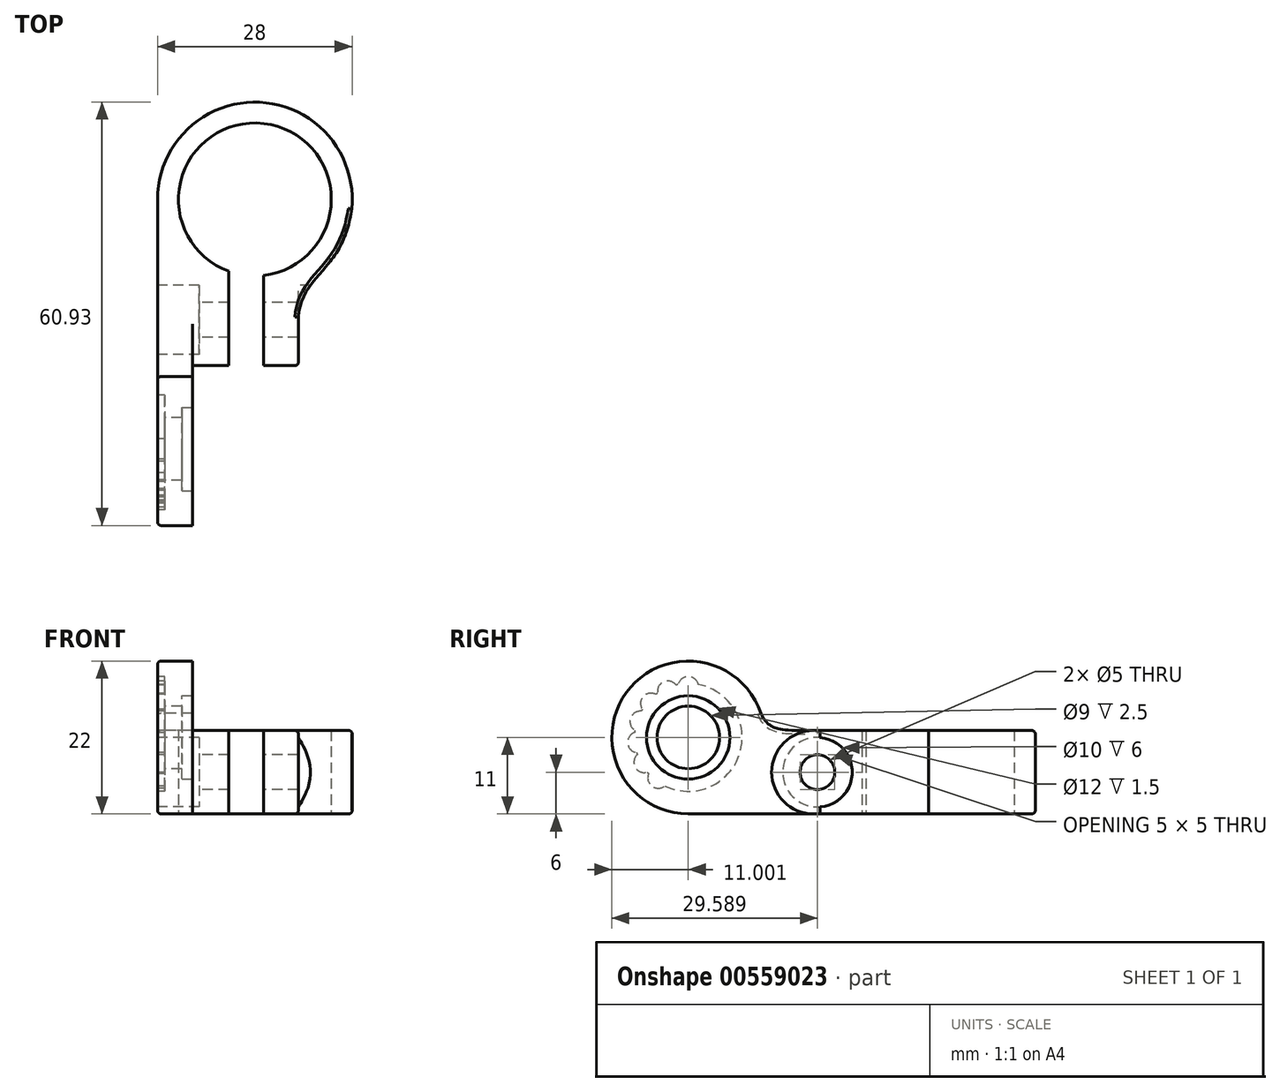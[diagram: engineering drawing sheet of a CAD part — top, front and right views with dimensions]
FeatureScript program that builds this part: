
annotation { "Feature Type Name" : "Feature", "Feature Type Description" : "" }
export const myFeature = defineFeature(function(context is Context, id is Id, definition is map)
    precondition{}
    {
        {
            var Q0;
            Q0=qCreatedBy(makeId("Top.planeOp"),FACE);
            var sketch = newSketch(context, id + "F0", { "sketchPlane" : qUnion([Q0])});
            skArc(sketch, "E0", {"start": v(1.25, -10.93) * mm, "mid": v(1.28, 10.92) * mm, "end": v(-3.75, -10.34) * mm});
            skArc(sketch, "E1", {"start": v(13.93, -1.37) * mm, "mid": v(0.69, 13.98) * mm, "end": v(-14, 0) * mm});
            skLineSegment(sketch, "E2", {"start": v(-14, 0) * mm, "end": v(-14, -23.93) * mm});
            skFitSpline(sketch, "E3", {"points": [v(13.93, -1.37) * mm, v(6.25, -16.94) * mm], "startDerivative": vector(-3.88, -27.33) * mm, "endDerivative": vector(-1.43, -19.02) * mm});
            skLineSegment(sketch, "E4", {"start": v(6.25, -16.94) * mm, "end": v(6.25, -23.93) * mm});
            skLineSegment(sketch, "E5", {"start": v(6.25, -23.93) * mm, "end": v(1.25, -23.93) * mm});
            skLineSegment(sketch, "E6", {"start": v(1.25, -23.93) * mm, "end": v(1.25, -10.93) * mm});
            skLineSegment(sketch, "E7", {"start": v(-3.75, -10.34) * mm, "end": v(-3.75, -23.93) * mm});
            skLineSegment(sketch, "E8", {"start": v(-3.75, -23.93) * mm, "end": v(-14, -23.93) * mm});
            skSolve(sketch);
        }
        {
            var Q0;
            Q0=makeQuery(id+"F0.imprint","IMPRINT",FACE,{"disambiguationData":[TD([[makeQuery(id+"F0.imprint","IMPRINT",EDGE,{"derivedFrom":sQuery(id+"F0.wireOp",EDGE,"E0")}),-1.0]])]});
            extrude(context, id + "F1", {"entities" : qUnion([Q0]), "endBound" : BoundingType.SYMMETRIC, "depth" : 12 * mm, "offsetDistance" : 25 * mm});
        }
        {
            var Q0;
            Q0=makeQuery(id+"F1.opExtrude","SWEPT_FACE",FACE,{"disambiguationData":[OSD([sQuery(id+"F0.wireOp",EDGE,"E2")])]});
            var sketch = newSketch(context, id + "F2", { "sketchPlane" : qUnion([Q0])});
            skLineSegment(sketch, "E9", {"start": v(23.93, -6) * mm, "end": v(35.93, -6) * mm});
            skCircle(sketch, "E10", {"center": v(35.93, 5) * mm, "radius": 11 * mm});
            skFitSpline(sketch, "E11", {"points": [v(19.13, 6) * mm, v(24.07, 6.72) * mm, v(26.04, 9.82) * mm], "startDerivative": vector(19.83, 0) * mm, "endDerivative": vector(5.27, 14.74) * mm});
            skSolve(sketch);
        }
        {
            var Q0;
            Q0 = qSketchRegion(id + "F2", true);
            var Q1;
            {var subQ7=sQuery(id+"F2.wireOp",EDGE,"E9");Q1=makeQuery(id+"F2.imprint","IMPRINT",FACE,{"disambiguationData":[TD([[makeQuery(id+"F2.imprint","IMPRINT",EDGE,{"derivedFrom":subQ7}),1.0]])]});}
            extrude(context, id + "F3", {"entities" : qUnion([Q0, Q1]), "operationType" : NewBodyOperationType.ADD, "oppositeDirection" : true, "depth" : 5 * mm, "offsetDistance" : 25 * mm});
        }
        {
            var Q0;
            {var subQ0=sQuery(id+"F0.wireOp",EDGE,"E2");Q0=makeQuery(id+"F3.boolean.opBoolean","MERGE",FACE,{"derivedFrom":[makeQuery(id+"F1.opExtrude","SWEPT_FACE",FACE,{"disambiguationData":[OSD([subQ0])]}),makeQuery(id+"F3.opExtrude","CAP_FACE",FACE,{"disambiguationData":[OSD([subQ0,sQuery(id+"F0.wireOp",EDGE,"E8"),sQuery(id+"F2.wireOp",EDGE,"E9"),sQuery(id+"F2.wireOp",EDGE,"E10"),sQuery(id+"F2.wireOp",EDGE,"E11")])],"isStart":true})]});}
            var sketch = newSketch(context, id + "F4", { "sketchPlane" : qUnion([Q0])});
            skCircle(sketch, "E12", {"center": v(17.34, 0) * mm, "radius": 2.5 * mm});
            skCircle(sketch, "E13", {"center": v(17.34, 0) * mm, "radius": 5 * mm});
            skSolve(sketch);
        }
        {
            var Q0;
            Q0=makeQuery(id+"F4.imprint","IMPRINT",FACE,{"disambiguationData":[TD([[makeQuery(id+"F4.imprint","IMPRINT",EDGE,{"derivedFrom":sQuery(id+"F4.wireOp",EDGE,"E12")}),1.0]])]});
            extrude(context, id + "F5", {"entities" : qUnion([Q0]), "operationType" : NewBodyOperationType.REMOVE, "endBound" : BoundingType.THROUGH_ALL, "oppositeDirection" : true, "depth" : 25 * mm, "offsetDistance" : 25 * mm});
        }
        {
            var Q0;
            Q0 = qSketchRegion(id + "F4", true);
            extrude(context, id + "F6", {"entities" : qUnion([Q0]), "operationType" : NewBodyOperationType.REMOVE, "oppositeDirection" : true, "depth" : 6 * mm, "offsetDistance" : 25 * mm});
        }
        {
            var Q0;
            Q0=makeQuery(id+"F1.opExtrude","SWEPT_FACE",FACE,{"disambiguationData":[OSD([sQuery(id+"F0.wireOp",EDGE,"E4")])]});
            var sketch = newSketch(context, id + "F7", { "sketchPlane" : qUnion([Q0])});
            skCircle(sketch, "E14", {"center": v(-17.34, 0) * mm, "radius": 5 * mm});
            skSolve(sketch);
        }
        {
            var Q0;
            Q0 = qSketchRegion(id + "F7", true);
            extrude(context, id + "F8", {"entities" : qUnion([Q0]), "operationType" : NewBodyOperationType.REMOVE, "endBound" : BoundingType.THROUGH_ALL, "depth" : 25 * mm, "offsetDistance" : 25 * mm});
        }
        {
            var Q0;
            {var subQ0=sQuery(id+"F0.wireOp",EDGE,"E2");Q0=makeQuery(id+"F3.boolean.opBoolean","MERGE",FACE,{"derivedFrom":[makeQuery(id+"F1.opExtrude","SWEPT_FACE",FACE,{"disambiguationData":[OSD([subQ0])]}),makeQuery(id+"F3.opExtrude","CAP_FACE",FACE,{"disambiguationData":[OSD([subQ0,sQuery(id+"F0.wireOp",EDGE,"E8"),sQuery(id+"F2.wireOp",EDGE,"E9"),sQuery(id+"F2.wireOp",EDGE,"E10"),sQuery(id+"F2.wireOp",EDGE,"E11")])],"isStart":true})]});}
            var sketch = newSketch(context, id + "F9", { "sketchPlane" : qUnion([Q0])});
            skCircle(sketch, "E15", {"center": v(35.93, 5) * mm, "radius": 4.5 * mm});
            skArc(sketch, "E16", {"start": v(39.31, -1.97) * mm, "mid": v(41.16, -2.01) * mm, "end": v(41.65, -0.23) * mm});
            skArc(sketch, "E17", {"start": v(34.47, 12.61) * mm, "mid": v(28.57, 2.56) * mm, "end": v(39.31, -1.97) * mm});
            skArc(sketch, "E18.trimOffspring", {"start": v(37.38, 12.61) * mm, "mid": v(35.93, 13.75) * mm, "end": v(34.47, 12.61) * mm});
            skArc(sketch, "E19.trimOffspring", {"start": v(37.68, 12.55) * mm, "mid": v(37.53, 12.58) * mm, "end": v(37.38, 12.61) * mm});
            skArc(sketch, "E20.trimOffspring", {"start": v(40.34, 11.37) * mm, "mid": v(39.47, 13) * mm, "end": v(37.68, 12.55) * mm});
            skArc(sketch, "E21.trimOffspring", {"start": v(40.59, 11.2) * mm, "mid": v(40.46, 11.28) * mm, "end": v(40.34, 11.37) * mm});
            skArc(sketch, "E22.trimOffspring", {"start": v(42.54, 9.04) * mm, "mid": v(42.4, 10.88) * mm, "end": v(40.59, 11.2) * mm});
            skArc(sketch, "E23.trimOffspring", {"start": v(42.7, 8.78) * mm, "mid": v(42.62, 8.9) * mm, "end": v(42.54, 9.04) * mm});
            skArc(sketch, "E24.trimOffspring", {"start": v(43.61, 6.02) * mm, "mid": v(44.23, 7.76) * mm, "end": v(42.7, 8.78) * mm});
            skArc(sketch, "E25.trimOffspring", {"start": v(43.65, 5.72) * mm, "mid": v(43.63, 5.87) * mm, "end": v(43.61, 6.02) * mm});
            skArc(sketch, "E26.trimOffspring", {"start": v(43.37, 2.82) * mm, "mid": v(44.64, 4.16) * mm, "end": v(43.65, 5.72) * mm});
            skArc(sketch, "E27.trimOffspring", {"start": v(43.27, 2.53) * mm, "mid": v(43.32, 2.67) * mm, "end": v(43.37, 2.82) * mm});
            skArc(sketch, "E28.trimOffspring", {"start": v(41.65, -0.23) * mm, "mid": v(41.75, -0.12) * mm, "end": v(41.85, 0) * mm});
            skArc(sketch, "E29.trimOffspring", {"start": v(41.85, 0) * mm, "mid": v(43.55, 0.7) * mm, "end": v(43.27, 2.53) * mm});
            skSolve(sketch);
        }
        {
            var Q0;
            Q0 = qSketchRegion(id + "F9", true);
            var Q1;
            Q1=makeQuery(id+"F9.imprint","IMPRINT",FACE,{"disambiguationData":[TD([[makeQuery(id+"F9.imprint","IMPRINT",EDGE,{"derivedFrom":sQuery(id+"F9.wireOp",EDGE,"E15")}),-1.0]])]});
            var Q2;
            {var subQ0=sQuery(id+"F9.wireOp",EDGE,"fbPnNNW9-PMxX-t2PX-k55c-5nS3xq7yzQ3p");var subQ1=sQuery(id+"F9.wireOp",EDGE,"QZW2g8Qc-ykgd-0s4w-dwwp-Ej2pU9XGU9IL");var subQ2=makeQuery(id+"F9.imprint","INTERSECT",VERTEX,{"disambiguationData":[OD(0.0)],"derivedFrom":[subQ1,subQ0]});Q2=makeQuery(id+"F9.imprint","IMPRINT",FACE,{"disambiguationData":[TD([[makeQuery(id+"F9.imprint","IMPRINT",EDGE,{"disambiguationData":[TD([[subQ2,1.0]])],"derivedFrom":subQ1}),1.0]])]});}
            var Q3;
            {var subQ0=sQuery(id+"F9.wireOp",EDGE,"yLPPB9Eb-vPD5-GLMI-5RPp-IEYl9C8609n6");var subQ1=sQuery(id+"F9.wireOp",EDGE,"QZW2g8Qc-ykgd-0s4w-dwwp-Ej2pU9XGU9IL");var subQ2=makeQuery(id+"F9.imprint","INTERSECT",VERTEX,{"disambiguationData":[OD(0.0)],"derivedFrom":[subQ1,subQ0]});Q3=makeQuery(id+"F9.imprint","IMPRINT",FACE,{"disambiguationData":[TD([[makeQuery(id+"F9.imprint","IMPRINT",EDGE,{"disambiguationData":[TD([[subQ2,-1.0]])],"derivedFrom":subQ1}),1.0]])]});}
            var Q4;
            {var subQ0=sQuery(id+"F9.wireOp",EDGE,"E16");var subQ1=sQuery(id+"F9.wireOp",EDGE,"QZW2g8Qc-ykgd-0s4w-dwwp-Ej2pU9XGU9IL");var subQ2=makeQuery(id+"F9.imprint","INTERSECT",VERTEX,{"disambiguationData":[OD(0.0)],"derivedFrom":[subQ1,subQ0]});Q4=makeQuery(id+"F9.imprint","IMPRINT",FACE,{"disambiguationData":[TD([[makeQuery(id+"F9.imprint","IMPRINT",EDGE,{"disambiguationData":[TD([[subQ2,-1.0]])],"derivedFrom":subQ1}),1.0]])]});}
            var Q5;
            {var subQ0=sQuery(id+"F9.wireOp",EDGE,"8HanLNPq-ip7b-hnWU-B5sB-qfkkRq3HLb1e");var subQ1=sQuery(id+"F9.wireOp",EDGE,"QZW2g8Qc-ykgd-0s4w-dwwp-Ej2pU9XGU9IL");var subQ2=makeQuery(id+"F9.imprint","INTERSECT",VERTEX,{"disambiguationData":[OD(0.0)],"derivedFrom":[subQ1,subQ0]});Q5=makeQuery(id+"F9.imprint","IMPRINT",FACE,{"disambiguationData":[TD([[makeQuery(id+"F9.imprint","IMPRINT",EDGE,{"disambiguationData":[TD([[subQ2,-1.0]])],"derivedFrom":subQ1}),1.0]])]});}
            var Q6;
            {var subQ0=sQuery(id+"F9.wireOp",EDGE,"G71yeFtQ-zlGd-nF3p-KKE1-QoE51yrrW6Fs");var subQ1=sQuery(id+"F9.wireOp",EDGE,"QZW2g8Qc-ykgd-0s4w-dwwp-Ej2pU9XGU9IL");var subQ2=makeQuery(id+"F9.imprint","INTERSECT",VERTEX,{"disambiguationData":[OD(0.0)],"derivedFrom":[subQ1,subQ0]});Q6=makeQuery(id+"F9.imprint","IMPRINT",FACE,{"disambiguationData":[TD([[makeQuery(id+"F9.imprint","IMPRINT",EDGE,{"disambiguationData":[TD([[subQ2,-1.0]])],"derivedFrom":subQ1}),1.0]])]});}
            var Q7;
            {var subQ0=sQuery(id+"F9.wireOp",EDGE,"8UitzcVi-eXTD-MqgP-6Jej-oq9UdkX41hCN");var subQ1=sQuery(id+"F9.wireOp",EDGE,"QZW2g8Qc-ykgd-0s4w-dwwp-Ej2pU9XGU9IL");var subQ2=makeQuery(id+"F9.imprint","INTERSECT",VERTEX,{"disambiguationData":[OD(0.0)],"derivedFrom":[subQ1,subQ0]});Q7=makeQuery(id+"F9.imprint","IMPRINT",FACE,{"disambiguationData":[TD([[makeQuery(id+"F9.imprint","IMPRINT",EDGE,{"disambiguationData":[TD([[subQ2,-1.0]])],"derivedFrom":subQ1}),1.0]])]});}
            var Q8;
            {var subQ0=sQuery(id+"F9.wireOp",EDGE,"bhop12Ne-FdNS-1RI7-3D0L-sXM0d9xyUDR8");var subQ1=sQuery(id+"F9.wireOp",EDGE,"QZW2g8Qc-ykgd-0s4w-dwwp-Ej2pU9XGU9IL");var subQ2=makeQuery(id+"F9.imprint","INTERSECT",VERTEX,{"disambiguationData":[OD(0.0)],"derivedFrom":[subQ1,subQ0]});Q8=makeQuery(id+"F9.imprint","IMPRINT",FACE,{"disambiguationData":[TD([[makeQuery(id+"F9.imprint","IMPRINT",EDGE,{"disambiguationData":[TD([[subQ2,-1.0]])],"derivedFrom":subQ1}),1.0]])]});}
            extrude(context, id + "F10", {"entities" : qUnion([Q0, Q1, Q2, Q3, Q4, Q5, Q6, Q7, Q8]), "operationType" : NewBodyOperationType.REMOVE, "oppositeDirection" : true, "depth" : 1 * mm, "offsetDistance" : 25 * mm});
        }
        {
            var Q0;
            {var subQ0=sQuery(id+"F0.wireOp",EDGE,"E2");Q0=makeQuery(id+"F10.boolean.opBoolean","SPLIT",FACE,{"disambiguationData":[TD([makeQuery(id+"F10.opExtrude","SWEPT_FACE",FACE,{"disambiguationData":[OSD([sQuery(id+"F9.wireOp",EDGE,"E15")])]})])],"derivedFrom":makeQuery(id+"F3.boolean.opBoolean","MERGE",FACE,{"derivedFrom":[makeQuery(id+"F1.opExtrude","SWEPT_FACE",FACE,{"disambiguationData":[OSD([subQ0])]}),makeQuery(id+"F3.opExtrude","CAP_FACE",FACE,{"disambiguationData":[OSD([subQ0,sQuery(id+"F0.wireOp",EDGE,"E8"),sQuery(id+"F2.wireOp",EDGE,"E9"),sQuery(id+"F2.wireOp",EDGE,"E10"),sQuery(id+"F2.wireOp",EDGE,"E11")])],"isStart":true})]})});}
            extrude(context, id + "F11", {"entities" : qUnion([Q0]), "operationType" : NewBodyOperationType.REMOVE, "endBound" : BoundingType.THROUGH_ALL, "oppositeDirection" : true, "depth" : 25 * mm, "offsetDistance" : 25 * mm});
        }
        {
            var Q0;
            Q0=makeQuery(id+"F1.opExtrude","CAP_EDGE",EDGE,{"disambiguationData":[OSD([sQuery(id+"F0.wireOp",EDGE,"E5")])],"isStart":true});
            var Q1;
            Q1=makeQuery(id+"F1.opExtrude","CAP_EDGE",EDGE,{"disambiguationData":[OSD([sQuery(id+"F0.wireOp",EDGE,"E8")])],"isStart":true});
            var Q2;
            Q2=makeQuery(id+"F1.opExtrude","CAP_EDGE",EDGE,{"disambiguationData":[OSD([sQuery(id+"F0.wireOp",EDGE,"E8")])],"isStart":false});
            var Q3;
            Q3=makeQuery(id+"F1.opExtrude","CAP_EDGE",EDGE,{"disambiguationData":[OSD([sQuery(id+"F0.wireOp",EDGE,"E5")])],"isStart":false});
            fillet(context, id + "F12", {"entities" : qUnion([Q0, Q1, Q2, Q3]), "radius" : 6 * mm, "tangentPropagation" : true, "allowEdgeOverflow" : false});
        }
        {
            var Q0;
            Q0=makeQuery(id+"F12.opFillet","BLEND_EDGE",EDGE,{"blendedFrom":[makeQuery(id+"F1.opExtrude","CAP_EDGE",EDGE,{"disambiguationData":[OSD([sQuery(id+"F0.wireOp",EDGE,"E5")])],"isStart":false}),makeQuery(id+"F8.boolean.opBoolean","MERGE",FACE,{"derivedFrom":[makeQuery(id+"F1.opExtrude","SWEPT_FACE",FACE,{"disambiguationData":[OSD([sQuery(id+"F0.wireOp",EDGE,"E4")])]}),makeQuery(id+"F8.opExtrude","CAP_FACE",FACE,{"disambiguationData":[OSD([sQuery(id+"F7.wireOp",EDGE,"E14")])],"isStart":true})]})],"blendedInto":[makeQuery(id+"F8.boolean.opBoolean","MERGE",FACE,{"derivedFrom":[makeQuery(id+"F1.opExtrude","SWEPT_FACE",FACE,{"disambiguationData":[OSD([sQuery(id+"F0.wireOp",EDGE,"E4")])]}),makeQuery(id+"F8.opExtrude","CAP_FACE",FACE,{"disambiguationData":[OSD([sQuery(id+"F7.wireOp",EDGE,"E14")])],"isStart":true})]})]});
            var Q1;
            Q1=makeQuery(id+"F1.opExtrude","CAP_EDGE",EDGE,{"disambiguationData":[OSD([sQuery(id+"F0.wireOp",EDGE,"E4")])],"isStart":true});
            var Q2;
            Q2=makeQuery(id+"F1.opExtrude","CAP_EDGE",EDGE,{"disambiguationData":[OSD([sQuery(id+"F0.wireOp",EDGE,"E3")])],"isStart":true});
            var Q3;
            Q3=makeQuery(id+"F1.opExtrude","CAP_EDGE",EDGE,{"disambiguationData":[OSD([sQuery(id+"F0.wireOp",EDGE,"E4")])],"isStart":false});
            var Q4;
            Q4=makeQuery(id+"F1.opExtrude","CAP_EDGE",EDGE,{"disambiguationData":[OSD([sQuery(id+"F0.wireOp",EDGE,"E3")])],"isStart":false});
            var Q5;
            Q5=makeQuery(id+"F1.opExtrude","CAP_EDGE",EDGE,{"disambiguationData":[OSD([sQuery(id+"F0.wireOp",EDGE,"E1")])],"isStart":true});
            var Q6;
            Q6=makeQuery(id+"F1.opExtrude","CAP_EDGE",EDGE,{"disambiguationData":[OSD([sQuery(id+"F0.wireOp",EDGE,"E1")])],"isStart":false});
            var Q7;
            Q7=makeQuery(id+"F3.boolean.opBoolean","MERGE",EDGE,{"derivedFrom":[makeQuery(id+"F1.opExtrude","CAP_EDGE",EDGE,{"disambiguationData":[OSD([sQuery(id+"F0.wireOp",EDGE,"E2")])],"isStart":true}),makeQuery(id+"F3.opExtrude","CAP_EDGE",EDGE,{"disambiguationData":[OSD([sQuery(id+"F2.wireOp",EDGE,"E9")])],"isStart":true})]});
            var Q8;
            Q8=makeQuery(id+"F3.opExtrude","CAP_EDGE",EDGE,{"disambiguationData":[OSD([sQuery(id+"F2.wireOp",EDGE,"E10")])],"isStart":true});
            var Q9;
            Q9=makeQuery(id+"F3.opExtrude","CAP_EDGE",EDGE,{"disambiguationData":[OSD([sQuery(id+"F2.wireOp",EDGE,"E11")])],"isStart":true});
            var Q10;
            Q10=makeQuery(id+"F1.opExtrude","CAP_EDGE",EDGE,{"disambiguationData":[OSD([sQuery(id+"F0.wireOp",EDGE,"E2")])],"isStart":false});
            fillet(context, id + "F13", {"entities" : qUnion([Q0, Q1, Q2, Q3, Q4, Q5, Q6, Q7, Q8, Q9, Q10]), "radius" : 0.5 * mm, "tangentPropagation" : true, "allowEdgeOverflow" : false});
        }
        {
            var Q0;
            Q0=makeQuery(id+"F3.opExtrude","CAP_FACE",FACE,{"disambiguationData":[OSD([sQuery(id+"F0.wireOp",EDGE,"E2"),sQuery(id+"F0.wireOp",EDGE,"E8"),sQuery(id+"F2.wireOp",EDGE,"E9"),sQuery(id+"F2.wireOp",EDGE,"E10"),sQuery(id+"F2.wireOp",EDGE,"E11")])],"isStart":false});
            var sketch = newSketch(context, id + "F14", { "sketchPlane" : qUnion([Q0])});
            skCircle(sketch, "E30", {"center": v(-35.93, 5) * mm, "radius": 6 * mm});
            skSolve(sketch);
        }
        {
            var Q0;
            Q0=makeQuery(id+"F14.imprint","IMPRINT",FACE,{"disambiguationData":[TD([[makeQuery(id+"F14.imprint","IMPRINT",EDGE,{"derivedFrom":sQuery(id+"F14.wireOp",EDGE,"E30")}),1.0]])]});
            var Q1;
            Q1=sQuery(id+"F14.wireOp",EDGE,"E30");
            extrude(context, id + "F15", {"entities" : qUnion([Q0]), "operationType" : NewBodyOperationType.REMOVE, "surfaceEntities" : qUnion([Q1]), "oppositeDirection" : true, "depth" : 1.5 * mm, "offsetDistance" : 25 * mm});
        }
    });
